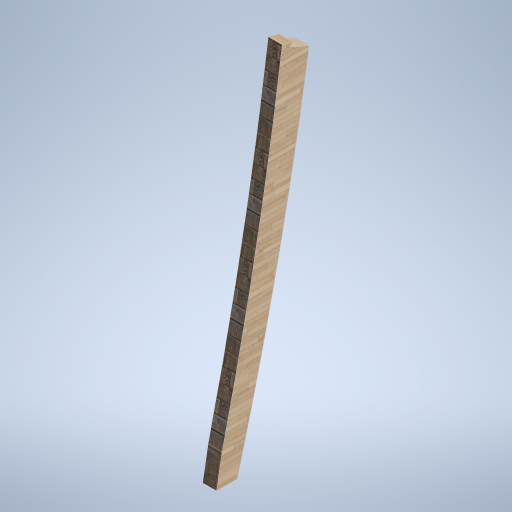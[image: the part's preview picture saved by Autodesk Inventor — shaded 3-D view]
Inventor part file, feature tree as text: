
AUTODESK INVENTOR PART (.ipt)
format: ipt  version: 2024.2 (Build 282272000, 272)  size: 321,536 bytes
history: native  units: in
note: dims shown in document units (in); Inventor stores cm internally (conversion verified against a paired STEP export)
features: other x3, sketch x1
ambient origin geometry x8: Origin, YZ Plane, XZ Plane, XY Plane, X Axis, Y Axis, Z Axis, Center Point
bodies: Solid1 (feature_tree)
feature tree (4):
  other  "side_curve_beam_02.ipt"
  other  "Solid1::side_curve_beam_02.ipt"
  other  "TaggingFeature1"
  sketch  "Sketch1"  dims[d0=0.3937in]
